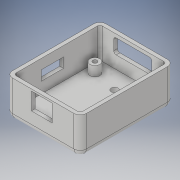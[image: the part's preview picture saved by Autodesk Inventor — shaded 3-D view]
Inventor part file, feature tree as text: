
AUTODESK INVENTOR PART (.ipt)
format: ipt  version: 2019.4 (Build 234330000, 330)  size: 245,760 bytes
history: native  units: mm
features: extrude x7, sketch x7, fillet x5, plane x1
ambient origin geometry x8: Origin, YZ Plane, XZ Plane, XY Plane, X Axis, Y Axis, Z Axis, Center Point
bodies: Solid1 (feature_tree)
feature tree (20):
  extrude  "Extrusion1"  Depth=76.0mm
  extrude  "Extrusion2"  Depth=3.0mm
  extrude  "Extrusion3"  Depth=54.0mm
  extrude  "Extrusion4"  Depth=25.0mm TaperAngle=0.0deg
  plane  "Work Plane1"
  fillet  "Fillet1"  Radius=15.0mm
  fillet  "Fillet2"  Radius=5.5mm
  fillet  "Fillet3"  Radius=5.5mm
  fillet  "Fillet4"  Radius=15.0mm
  extrude  "Extrusion8"  Depth=4.0mm
  fillet  "Fillet7"  Radius=7.0mm
  extrude  "Extrusion9"  Depth=3.5mm
  extrude  "Extrusion10"  Depth=8.0mm TaperAngle=0.0deg
  sketch  "Sketch1"  dims[d0=60.0mm d1=76.0mm]
  sketch  "Sketch2"  dims[d2=30.0mm d3=0.0mm d4=3.0mm]
  sketch  "Sketch3"  dims[d5=3.0mm d6=54.0mm]
  sketch  "Sketch4"  dims[d7=70.0mm d8=25.0mm d9=0.0mm d10=15.0mm d12=5.5mm d13=5.5mm d14=15.0mm d15=0.0mm]
  sketch  "Sketch8"  dims[d16=8.0mm d17=4.0mm d18=7.0mm]
  sketch  "Sketch9"  dims[d19=20.0mm d21=55.0mm d22=20.0mm d24=38.0mm d27=3.5mm]
  sketch  "Sketch10"  dims[d28=20.0mm d30=55.0mm d31=20.0mm d33=38.0mm d36=8.0mm d37=0.0mm d67=-50.0mm d78=5.0mm d79=5.0mm d80=2.0mm d81=2.0mm d85=27.0mm d86=15.0mm d87=14.75mm d88=2.73mm d89=31.0mm d90=12.0mm d91=10.0mm d92=0.0mm d93=2.0mm d94=32.5mm d95=8.0mm d96=18.0mm d97=8.0mm d98=3.0mm d99=0.0mm d100=20.38mm d101=1.5mm d102=17.0mm d103=14.0mm d104=3.0mm d105=0.0mm]
